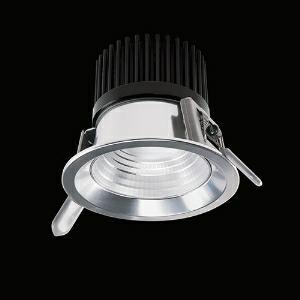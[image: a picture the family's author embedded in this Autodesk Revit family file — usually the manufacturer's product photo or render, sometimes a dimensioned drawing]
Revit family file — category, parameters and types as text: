
# Revit family: spectral_myral_myral_3500-830-f
name_source: partatom
category: Lighting Fixtures
revit_build: Autodesk Revit 2016 (Build: 20150220_1215(x64)
units: mm (PartAtom-declared; Revit-internal decimal feet)

## family parameters
Cut with Voids When Loaded = No
Host = Face
Light Source = No
Part Type = Normal
Room Calculation Point = No
Round Connector Dimension = Use Diameter
Shared = No

## types (1)
- SPECTRAL MYRAL (1 x )
    Apparent Load = 0 VA
    Approval mark = CE
    CIE Flux Codes = 81 99 100 100 100
    Control Gear = Electronic transformer
    Default Elevation = 1800 mm
    Description = SPG0320186
MYRAL recessed spot

Design:
    Height = 0 mm  [stored 0 ft]
    Lamp = 1 x
    Lamp count = 1
    Length = 120 mm
    Luminous efficacy = 0 lm/W
    Manufacturer = Ridi
    ModVariant = No
    Model = MYRAL 3500-830-F
    Mounting Place = Ceiling
    Mounting Type = Recessed
    Number of Poles = 1
    OnlyDefault = Yes
    Power Factor = 1
    Product Name = SPECTRAL MYRAL
    Product group = Downlight recessed
    ProductGroupID = 400
    Protection Class = Protection class
    Protection Degree = IP 20
    RlxData = <blob elided: 38881 chars, md5=abe8cb9b>
    Socket = socket
    Standby Power = 0 W
    System Light Flux = 0 lm
    System Power = 0 W
    Type Image = myral_04.jpg
    URL = http://reluxnet.relux.com
    VarID = ---
    Voltage = 0 V
    Weight = 0.00 kg
    Width = 0 mm  [stored 0 ft]

note: [stored X ft] marks values corroborated as IEEE doubles in the binary element streams (Revit-internal decimal feet)

## geometry (parser evidence)
native form markers: Sweep x10
no freeform markers — native parametric forms only
